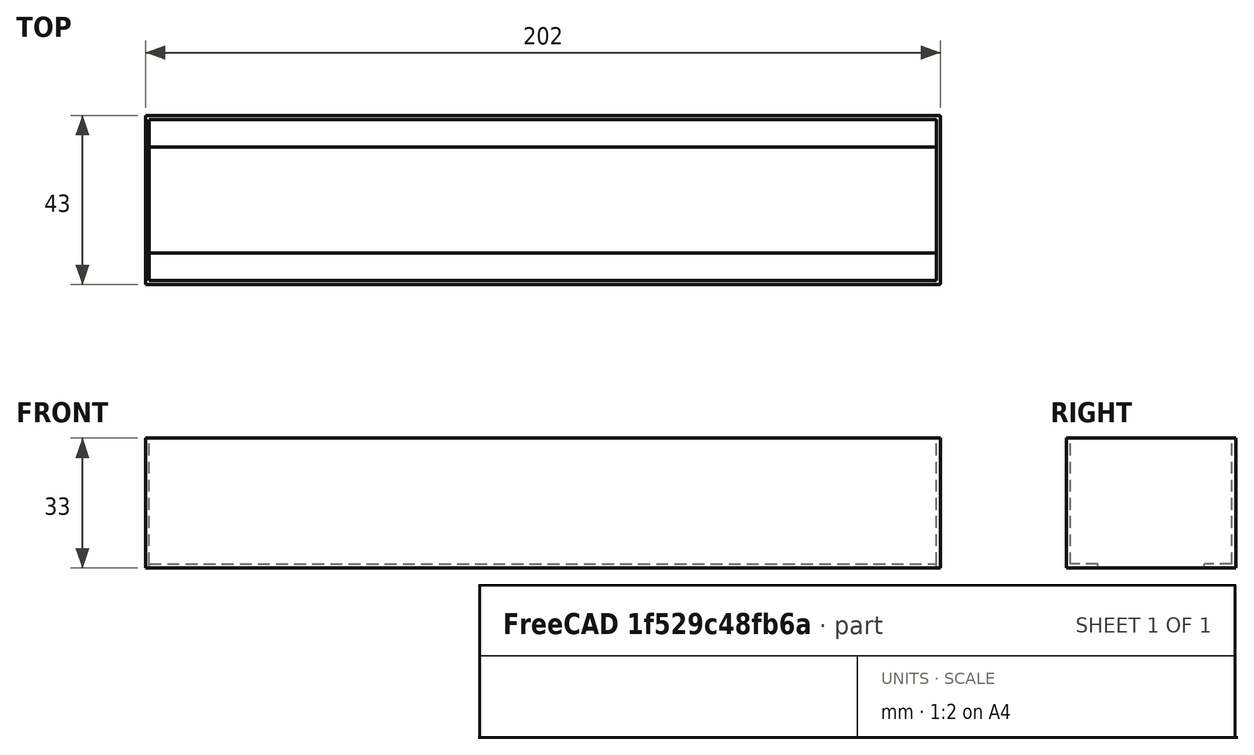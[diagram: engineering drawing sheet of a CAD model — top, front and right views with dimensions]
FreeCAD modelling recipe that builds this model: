
FCSTD DOCUMENT  (FreeCAD 0.18R4 (GitTag))
Label: adventure
License: All rights reserved
LicenseURL: http://en.wikipedia.org/wiki/All_rights_reserved
objects: Part::Box×4, Part::Cut×1, Part::MultiFuse×1
note: 6 computed .brp shape members not serialized (recipe doc carries the construction recipe); baked Part::Feature solids carry a one-line shape summary decoded from their .brp

FEATURE [Part::Box] Box  label="Cube"
  AttacherType = Attacher::AttachEngine3D
  Height = 33
  Length = 202
  Width = 43
FEATURE [Part::Box] Box001  label="Cube001"
  AttacherType = Attacher::AttachEngine3D
  Height = 33
  Length = 200
  Placement = pos=(1,1,0) rot=(0,0,1;0rad)
  Width = 41
FEATURE [Part::Cut] Cut
  Base = -> Box
  Tool = -> Box001
FEATURE [Part::Box] Box002  label="Cube002"
  AttacherType = Attacher::AttachEngine3D
  Height = 1
  Length = 202
  Width = 8
FEATURE [Part::Box] Box003  label="Cube003"
  AttacherType = Attacher::AttachEngine3D
  Height = 1
  Length = 202
  Placement = pos=(0,35,0) rot=(0,0,1;0rad)
  Width = 8
FEATURE [Part::MultiFuse] Fusion
  Shapes = -> [Cut,Box002,Box003]
